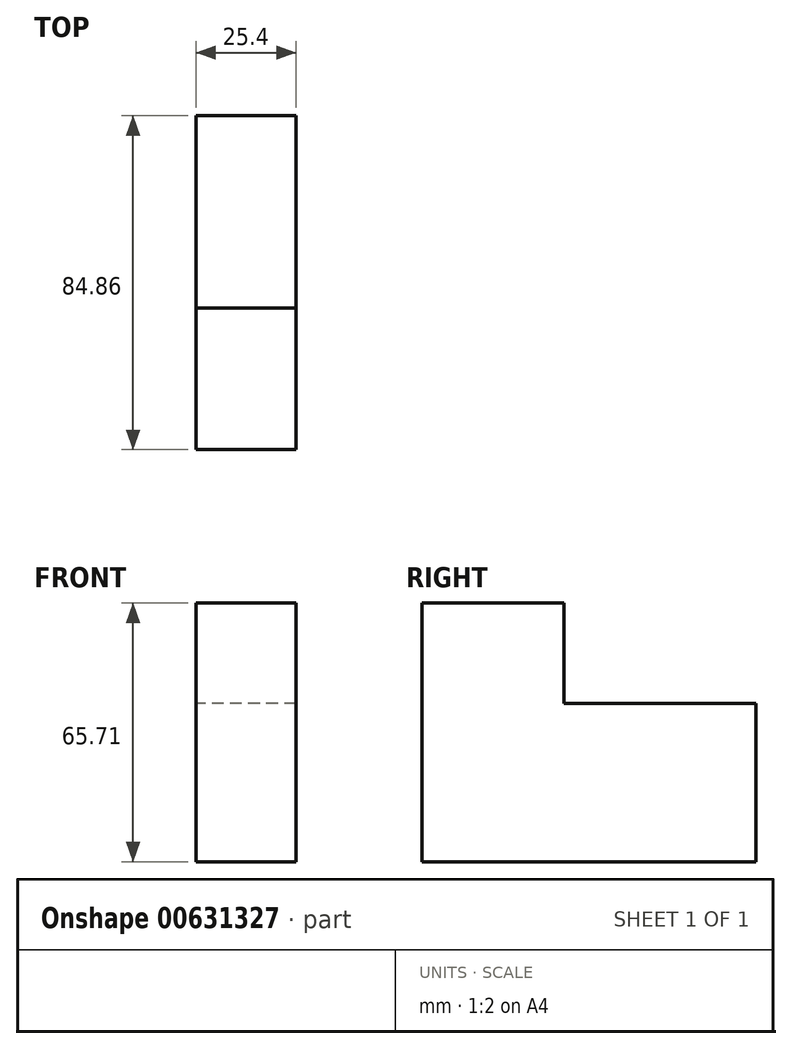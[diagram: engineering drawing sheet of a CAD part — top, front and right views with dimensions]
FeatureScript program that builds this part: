
annotation { "Feature Type Name" : "Feature", "Feature Type Description" : "" }
export const myFeature = defineFeature(function(context is Context, id is Id, definition is map)
    precondition{}
    {
        {
            var Q0;
            Q0=qCreatedBy(makeId("Right.planeOp"),FACE);
            var sketch = newSketch(context, id + "F0", { "sketchPlane" : qUnion([Q0])});
            skLineSegment(sketch, "E0.bottom", {"start": v(0, 0) * mm, "end": v(84.86, 0) * mm});
            skLineSegment(sketch, "E0.top", {"start": v(0, 40.23) * mm, "end": v(84.86, 40.23) * mm});
            skLineSegment(sketch, "E0.left", {"start": v(0, 0) * mm, "end": v(0, 40.23) * mm});
            skLineSegment(sketch, "E0.right", {"start": v(84.86, 0) * mm, "end": v(84.86, 40.23) * mm});
            skLineSegment(sketch, "E1.bottom", {"start": v(0, 40.23) * mm, "end": v(36.02, 40.23) * mm});
            skLineSegment(sketch, "E1.top", {"start": v(0, 65.7) * mm, "end": v(36.02, 65.7) * mm});
            skLineSegment(sketch, "E1.left", {"start": v(0, 40.23) * mm, "end": v(0, 65.7) * mm});
            skLineSegment(sketch, "E1.right", {"start": v(36.02, 40.23) * mm, "end": v(36.02, 65.7) * mm});
            skSolve(sketch);
        }
        {
            var Q0;
            Q0=qSketchRegion(id+"F0",true);
            extrude(context, id + "F1", {"entities" : qUnion([Q0]), "depth" : 25.4 * mm, "offsetDistance" : 25.4 * mm});
        }
    });
